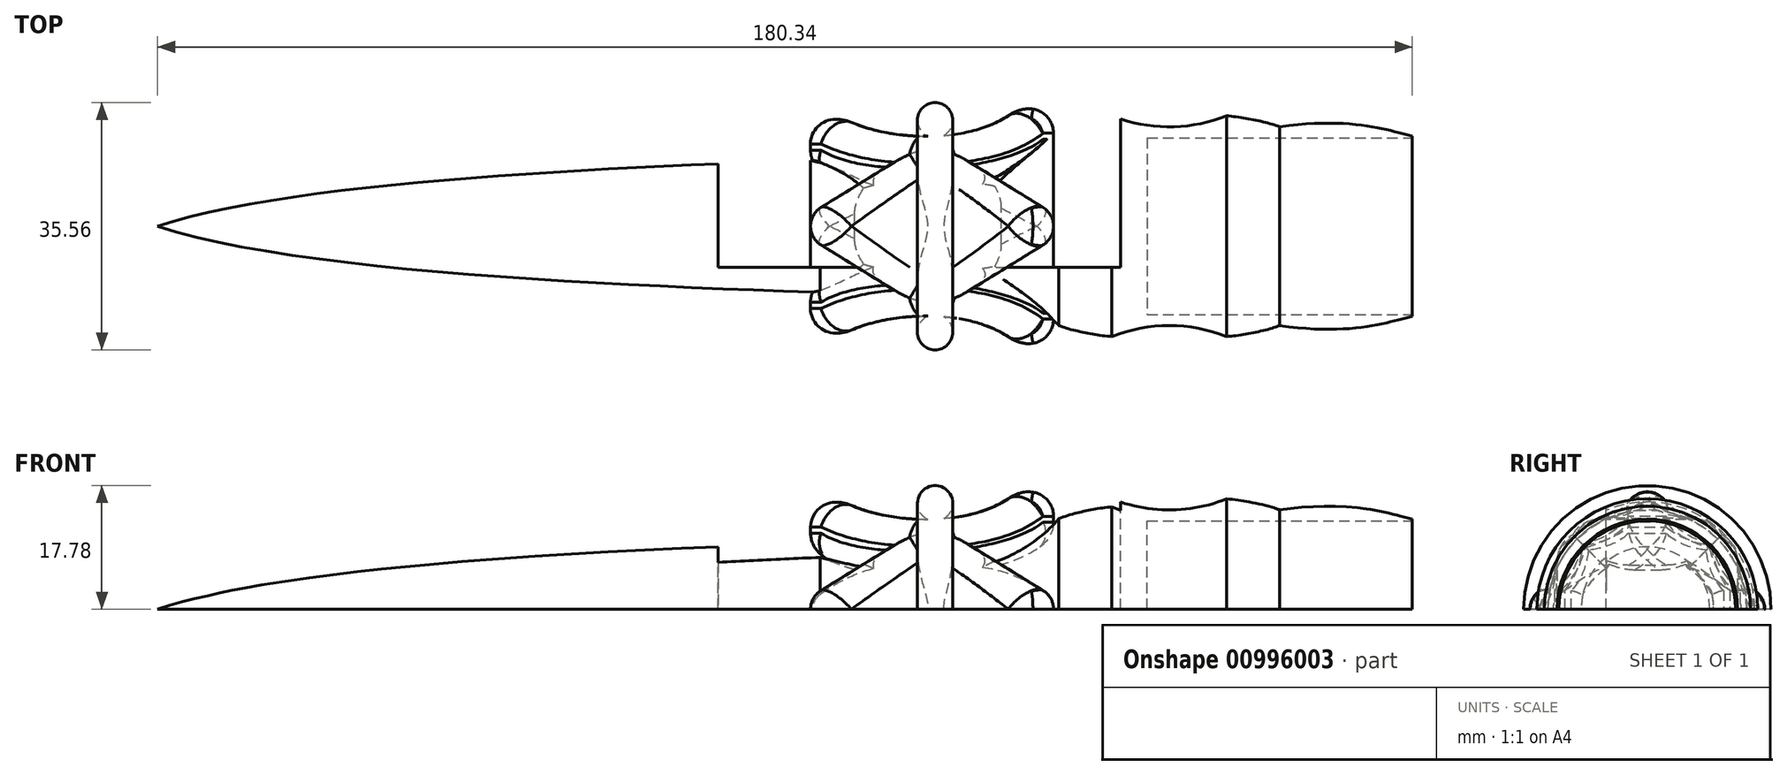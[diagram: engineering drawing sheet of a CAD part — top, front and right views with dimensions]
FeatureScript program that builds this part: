
annotation { "Feature Type Name" : "Feature", "Feature Type Description" : "" }
export const myFeature = defineFeature(function(context is Context, id is Id, definition is map)
    precondition{}
    {
        {
            var Q0;
            Q0=qCreatedBy(makeId("Top.planeOp"),FACE);
            var sketch = newSketch(context, id + "F0", { "sketchPlane" : qUnion([Q0])});
            skLineSegment(sketch, "E0", {"start": v(-2589.65, -19.48) * mm, "end": v(-2409.31, -19.48) * mm});
            skLineSegment(sketch, "E1", {"start": v(-2409.31, -19.48) * mm, "end": v(-2409.31, -6.52) * mm});
            skFitSpline(sketch, "E2", {"points": [v(-2409.31, -6.52) * mm, v(-2428.36, -5.19) * mm], "startDerivative": vector(-10.37, 2.38) * mm, "endDerivative": vector(-31.35, -4.48) * mm});
            skFitSpline(sketch, "E3", {"points": [v(-2428.36, -5.19) * mm, v(-2435.98, -3.6) * mm], "startDerivative": vector(-5.77, 2.19) * mm, "endDerivative": vector(-7.46, 0.63) * mm});
            skArc(sketch, "E4", {"start": v(-2452.5, -3.6) * mm, "mid": v(-2444.24, -5.2) * mm, "end": v(-2435.98, -3.6) * mm});
            skFitSpline(sketch, "E5.MirrorCS", {"points": [v(-2460.11, -5.19) * mm, v(-2452.5, -3.6) * mm], "startDerivative": vector(5.77, 2.19) * mm, "endDerivative": vector(7.46, 0.63) * mm});
            skFitSpline(sketch, "E6", {"points": [v(-2589.65, -19.48) * mm, v(-2494.4, -9.95) * mm], "startDerivative": vector(58.8, 19.45) * mm, "endDerivative": vector(95.3, 3.3) * mm});
            skFitSpline(sketch, "E7", {"points": [v(-2494.4, -9.95) * mm, v(-2460.11, -5.19) * mm], "startDerivative": vector(32.47, -6.47) * mm, "endDerivative": vector(23.9, 25.55) * mm});
            skSolve(sketch);
        }
        {
            var Q0;
            Q0 = qSketchRegion(id + "F0", true);
            var Q1;
            Q1=sQuery(id+"F0.wireOp",EDGE,"E0");
            revolve(context, id + "F1", {"surfaceOperationType" : NewSurfaceOperationType.NEW, "entities" : qUnion([Q0]), "axis" : qUnion([Q1]), "revolveType" : RevolveType.FULL});
        }
        {
            var Q0;
            Q0=qCreatedBy(makeId("Top.planeOp"),FACE);
            var sketch = newSketch(context, id + "F2", { "sketchPlane" : qUnion([Q0])});
            skFitSpline(sketch, "E8", {"points": [v(-2491.09, -3.98) * mm, v(-2466.75, -3.12) * mm], "startDerivative": vector(18.72, -10.04) * mm, "endDerivative": vector(17.87, 13.95) * mm});
            skCircle(sketch, "E9", {"center": v(-2493.04, -7.62) * mm, "radius": 4.13 * mm});
            skCircle(sketch, "E10", {"center": v(-2464.2, -6.37) * mm, "radius": 4.13 * mm});
            skFitSpline(sketch, "E11", {"points": [v(-2495.68, -10.8) * mm, v(-2461.28, -9.28) * mm], "startDerivative": vector(23.68, -19.68) * mm, "endDerivative": vector(18.21, 18.28) * mm});
            skSolve(sketch);
        }
        {
            var Q0;
            Q0 = qSketchRegion(id + "F2", true);
            extrude(context, id + "F3", {"entities" : qUnion([Q0]), "endBound" : BoundingType.SYMMETRIC, "depth" : 25.4 * mm, "offsetDistance" : 25.4 * mm});
        }
        {
            var Q0;
            Q0=qCreatedBy(makeId("Front.planeOp"),FACE);
            var sketch = newSketch(context, id + "F4", { "sketchPlane" : qUnion([Q0])});
            skLineSegment(sketch, "E12", {"start": v(-2460.88, 0) * mm, "end": v(-2495.8, 0) * mm, "construction": true});
            skLineSegment(sketch, "E13", {"start": v(-2478.34, -11.43) * mm, "end": v(-2478.34, 11.43) * mm, "construction": true});
            skArc(sketch, "E14", {"start": v(-2462.38, -2.7) * mm, "mid": v(-2461.28, -1.55) * mm, "end": v(-2460.88, 0) * mm});
            skArc(sketch, "E15", {"start": v(-2478.34, -11.43) * mm, "mid": v(-2476.6, -11.19) * mm, "end": v(-2475, -10.49) * mm});
            skLineSegment(sketch, "E16", {"start": v(-2475, -10.49) * mm, "end": v(-2462.38, -2.7) * mm});
            skArc(sketch, "E17.MirrorCS", {"start": v(-2478.34, 11.43) * mm, "mid": v(-2476.6, 11.19) * mm, "end": v(-2475, 10.49) * mm});
            skLineSegment(sketch, "E18.MirrorCS", {"start": v(-2475, 10.49) * mm, "end": v(-2462.38, 2.7) * mm});
            skArc(sketch, "E19.MirrorCS", {"start": v(-2462.38, 2.7) * mm, "mid": v(-2461.28, 1.55) * mm, "end": v(-2460.88, 0) * mm});
            skArc(sketch, "E20.MirrorCS", {"start": v(-2478.34, 11.43) * mm, "mid": v(-2480.07, 11.19) * mm, "end": v(-2481.67, 10.49) * mm});
            skLineSegment(sketch, "E21.MirrorCS", {"start": v(-2481.67, 10.49) * mm, "end": v(-2494.3, 2.7) * mm});
            skArc(sketch, "E22.MirrorCS", {"start": v(-2494.3, 2.7) * mm, "mid": v(-2495.4, 1.55) * mm, "end": v(-2495.8, 0) * mm});
            skArc(sketch, "E23.MirrorCS", {"start": v(-2494.3, -2.7) * mm, "mid": v(-2495.4, -1.55) * mm, "end": v(-2495.8, 0) * mm});
            skLineSegment(sketch, "E24.MirrorCS", {"start": v(-2481.67, -10.49) * mm, "end": v(-2494.3, -2.7) * mm});
            skArc(sketch, "E25.MirrorCS", {"start": v(-2478.34, -11.43) * mm, "mid": v(-2480.07, -11.19) * mm, "end": v(-2481.67, -10.49) * mm});
            skLineSegment(sketch, "E26.bottom", {"start": v(-2451.25, -31.68) * mm, "end": v(-2509.1, -31.68) * mm});
            skLineSegment(sketch, "E26.top", {"start": v(-2451.25, 38) * mm, "end": v(-2509.1, 38) * mm});
            skLineSegment(sketch, "E26.left", {"start": v(-2451.25, -31.68) * mm, "end": v(-2451.25, 38) * mm});
            skLineSegment(sketch, "E26.right", {"start": v(-2509.1, -31.68) * mm, "end": v(-2509.1, 38) * mm});
            skSolve(sketch);
        }
        {
            var Q0;
            Q0 = qSketchRegion(id + "F4", true);
            extrude(context, id + "F5", {"entities" : qUnion([Q0]), "operationType" : NewBodyOperationType.REMOVE, "depth" : 25.4 * mm, "offsetDistance" : 25.4 * mm});
        }
        {
            var Q0;
            Q0=makeQuery(id+"F5.boolean.opBoolean","INTERSECT",EDGE,{"derivedFrom":[makeQuery(id+"F3.opExtrude","SWEPT_FACE",FACE,{"disambiguationData":[OSD([sQuery(id+"F2.wireOp",EDGE,"E8")])]}),makeQuery(id+"F5.opExtrude","SWEPT_FACE",FACE,{"disambiguationData":[OSD([sQuery(id+"F4.wireOp",EDGE,"E21.MirrorCS")])]})]});
            var Q1;
            Q1=makeQuery(id+"F5.boolean.opBoolean","INTERSECT",EDGE,{"derivedFrom":[makeQuery(id+"F3.opExtrude","SWEPT_FACE",FACE,{"disambiguationData":[OSD([sQuery(id+"F2.wireOp",EDGE,"E11")])]}),makeQuery(id+"F5.opExtrude","SWEPT_FACE",FACE,{"disambiguationData":[OSD([sQuery(id+"F4.wireOp",EDGE,"E21.MirrorCS")])]})]});
            fillet(context, id + "F6", {"entities" : qUnion([Q0, Q1]), "radius" : 3.8 * mm, "tangentPropagation" : true, "allowEdgeOverflow" : false});
        }
        {
            var Q0;
            Q0=makeQuery(id+"F3.opExtrude","SWEPT_BODY",BODY,{"disambiguationData":[OSD([sQuery(id+"F2.wireOp",EDGE,"E8"),sQuery(id+"F2.wireOp",EDGE,"E9"),sQuery(id+"F2.wireOp",EDGE,"E10"),sQuery(id+"F2.wireOp",EDGE,"E11")])]});
            var Q1;
            Q1=sQuery(id+"F0.wireOp",EDGE,"E0");
            circularPattern(context, id + "F7", {"operationType" : NewBodyOperationType.ADD, "entities" : qUnion([Q0]), "axis" : qUnion([Q1]), "angle" : 360 * degree, "instanceCount" : 4, "equalSpace" : true});
        }
        {
            var Q0;
            Q0=qCreatedBy(makeId("Top.planeOp"),FACE);
            var sketch = newSketch(context, id + "F8", { "sketchPlane" : qUnion([Q0])});
            skCircle(sketch, "E27", {"center": v(-2477.9, -4.24) * mm, "radius": 2.54 * mm});
            skSolve(sketch);
        }
        {
            var Q0;
            Q0 = qSketchRegion(id + "F8", true);
            var Q1;
            Q1=sQuery(id+"F0.wireOp",EDGE,"E0");
            revolve(context, id + "F9", {"operationType" : NewBodyOperationType.ADD, "surfaceOperationType" : NewSurfaceOperationType.NEW, "entities" : qUnion([Q0]), "axis" : qUnion([Q1]), "revolveType" : RevolveType.FULL});
        }
        {
            var Q0;
            Q0=makeQuery(id+"F1.opRevolve","SWEPT_FACE",FACE,{"disambiguationData":[OSD([sQuery(id+"F0.wireOp",EDGE,"E1")])]});
            var sketch = newSketch(context, id + "F10", { "sketchPlane" : qUnion([Q0])});
            skCircle(sketch, "E28", {"center": v(-19.48, 0) * mm, "radius": 12.7 * mm});
            skSolve(sketch);
        }
        {
            var Q0;
            Q0 = qSketchRegion(id + "F10", true);
            extrude(context, id + "F11", {"entities" : qUnion([Q0]), "operationType" : NewBodyOperationType.REMOVE, "oppositeDirection" : true, "depth" : 38.1 * mm, "offsetDistance" : 25.4 * mm});
        }
        {
            var Q0;
            Q0=qCreatedBy(makeId("Top.planeOp"),FACE);
            var sketch = newSketch(context, id + "F12", { "sketchPlane" : qUnion([Q0])});
            skLineSegment(sketch, "E29.bottom", {"start": v(-2607.43, 19.28) * mm, "end": v(-2374.94, 19.28) * mm});
            skLineSegment(sketch, "E29.top", {"start": v(-2607.43, -73.84) * mm, "end": v(-2374.94, -73.84) * mm});
            skLineSegment(sketch, "E29.left", {"start": v(-2607.43, 19.28) * mm, "end": v(-2607.43, -73.84) * mm});
            skLineSegment(sketch, "E29.right", {"start": v(-2374.94, 19.28) * mm, "end": v(-2374.94, -73.84) * mm});
            skSolve(sketch);
        }
        {
            var Q0;
            Q0 = qSketchRegion(id + "F12", true);
            extrude(context, id + "F13", {"entities" : qUnion([Q0]), "operationType" : NewBodyOperationType.REMOVE, "oppositeDirection" : true, "depth" : 25.4 * mm, "offsetDistance" : 25.4 * mm});
        }
    });
